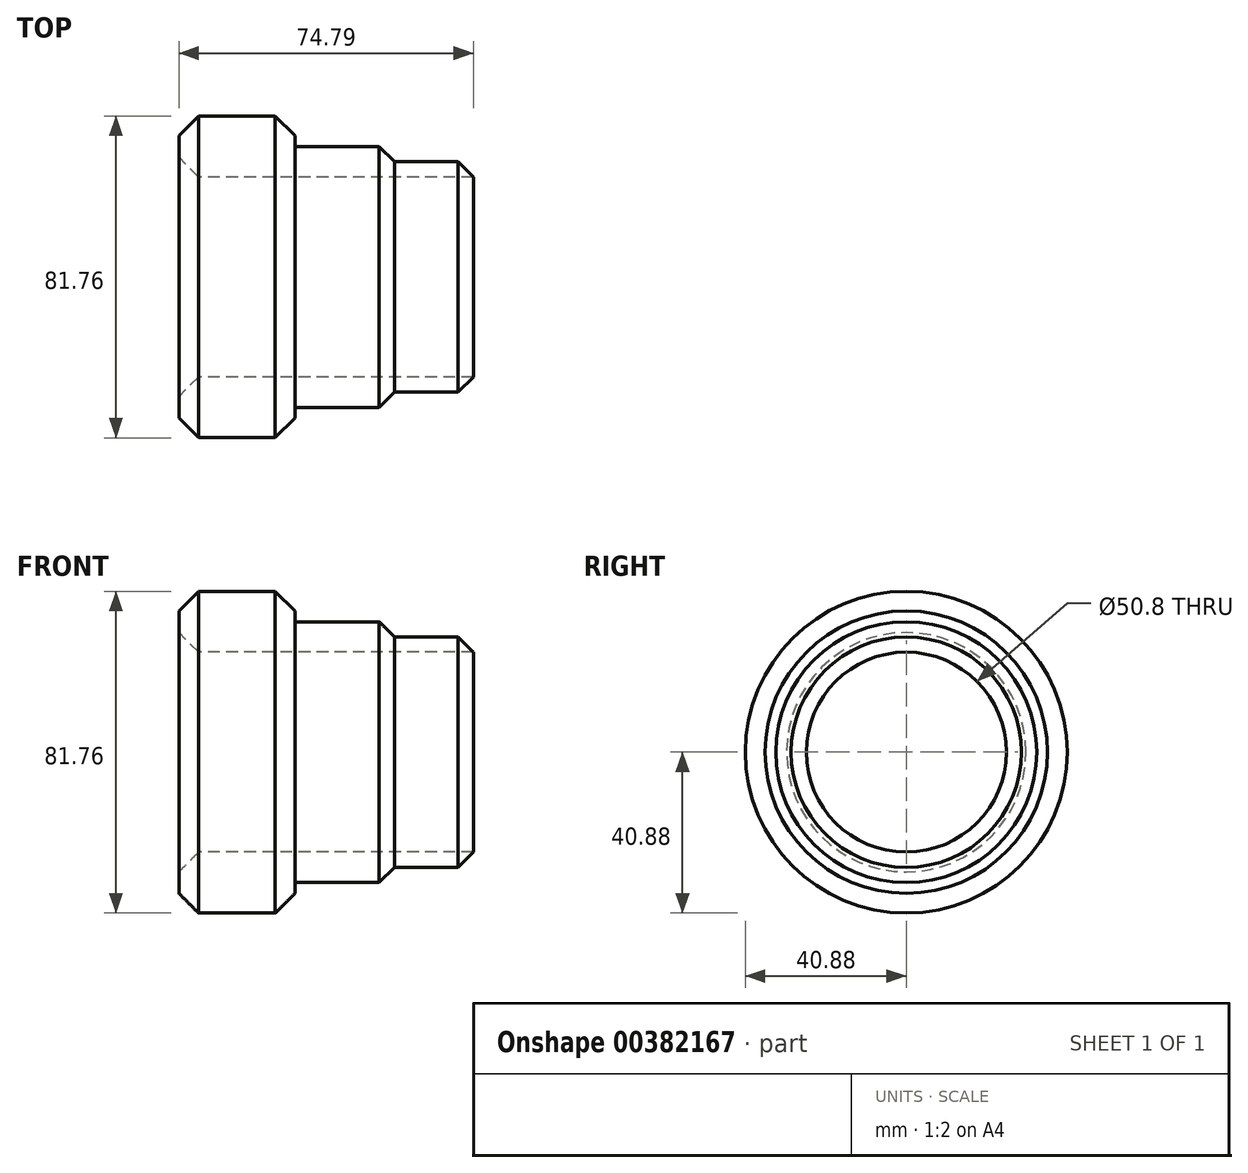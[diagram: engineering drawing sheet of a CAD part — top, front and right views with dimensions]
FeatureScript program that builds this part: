
annotation { "Feature Type Name" : "Feature", "Feature Type Description" : "" }
export const myFeature = defineFeature(function(context is Context, id is Id, definition is map)
    precondition{}
    {
        {
            var Q0;
            Q0=qCreatedBy(makeId("Front.planeOp"),FACE);
            var sketch = newSketch(context, id + "F0", { "sketchPlane" : qUnion([Q0])});
            skLineSegment(sketch, "E0", {"start": v(-50, 0) * mm, "end": v(50, 0) * mm, "construction": true});
            skLineSegment(sketch, "E1.bottom", {"start": v(-50.07, 40.88) * mm, "end": v(-20.58, 40.88) * mm});
            skLineSegment(sketch, "E1.top", {"start": v(-50.07, 25.4) * mm, "end": v(-20.58, 25.4) * mm});
            skLineSegment(sketch, "E1.left", {"start": v(-50.07, 40.88) * mm, "end": v(-50.07, 25.4) * mm});
            skLineSegment(sketch, "E1.right", {"start": v(-20.58, 40.88) * mm, "end": v(-20.58, 25.4) * mm});
            skLineSegment(sketch, "E2.bottom", {"start": v(-20.58, 33.14) * mm, "end": v(5.83, 33.14) * mm});
            skLineSegment(sketch, "E2.top", {"start": v(-20.58, 25.4) * mm, "end": v(5.83, 25.4) * mm});
            skLineSegment(sketch, "E2.left", {"start": v(-20.58, 33.14) * mm, "end": v(-20.58, 25.4) * mm});
            skLineSegment(sketch, "E2.right", {"start": v(5.83, 33.14) * mm, "end": v(5.83, 25.4) * mm});
            skLineSegment(sketch, "E3.bottom", {"start": v(5.83, 29.27) * mm, "end": v(25.86, 29.27) * mm});
            skLineSegment(sketch, "E3.top", {"start": v(5.83, 25.4) * mm, "end": v(25.86, 25.4) * mm});
            skLineSegment(sketch, "E3.left", {"start": v(5.83, 29.27) * mm, "end": v(5.83, 25.4) * mm});
            skLineSegment(sketch, "E3.right", {"start": v(25.86, 29.27) * mm, "end": v(25.86, 25.4) * mm});
            skSolve(sketch);
        }
        {
            var Q0;
            Q0 = qSketchRegion(id + "F0", true);
            var Q1;
            Q1=sQuery(id+"F0.wireOp",EDGE,"E0");
            revolve(context, id + "F1", {"entities" : qUnion([Q0]), "axis" : qUnion([Q1]), "revolveType" : RevolveType.FULL});
        }
        {
            var Q0;
            Q0=makeQuery(id+"F1.opRevolve","SWEPT_EDGE",EDGE,{"disambiguationData":[OSD([sQuery(id+"F0.wireOp",EDGE,"E1.bottom"),sQuery(id+"F0.wireOp",EDGE,"E1.left")])]});
            chamfer(context, id + "F2", {"entities" : qUnion([Q0]), "width" : 5 * mm, "tangentPropagation" : true});
        }
        {
            var Q0;
            Q0=makeQuery(id+"F1.opRevolve","SWEPT_EDGE",EDGE,{"disambiguationData":[OSD([sQuery(id+"F0.wireOp",EDGE,"E1.top"),sQuery(id+"F0.wireOp",EDGE,"E1.left")])]});
            var Q1;
            Q1=makeQuery(id+"F1.opRevolve","SWEPT_EDGE",EDGE,{"disambiguationData":[OSD([sQuery(id+"F0.wireOp",EDGE,"E1.bottom"),sQuery(id+"F0.wireOp",EDGE,"E1.right")])]});
            chamfer(context, id + "F3", {"entities" : qUnion([Q0, Q1]), "width" : 5 * mm, "tangentPropagation" : true});
        }
        {
            var Q0;
            Q0=makeQuery(id+"F1.opRevolve","SWEPT_EDGE",EDGE,{"disambiguationData":[OSD([sQuery(id+"F0.wireOp",EDGE,"E2.bottom"),sQuery(id+"F0.wireOp",EDGE,"E2.right")])]});
            var Q1;
            Q1=makeQuery(id+"F1.opRevolve","SWEPT_EDGE",EDGE,{"disambiguationData":[OSD([sQuery(id+"F0.wireOp",EDGE,"E3.bottom"),sQuery(id+"F0.wireOp",EDGE,"E3.right")])]});
            chamfer(context, id + "F4", {"entities" : qUnion([Q0, Q1]), "width" : 5 * mm, "tangentPropagation" : true});
        }
    });
